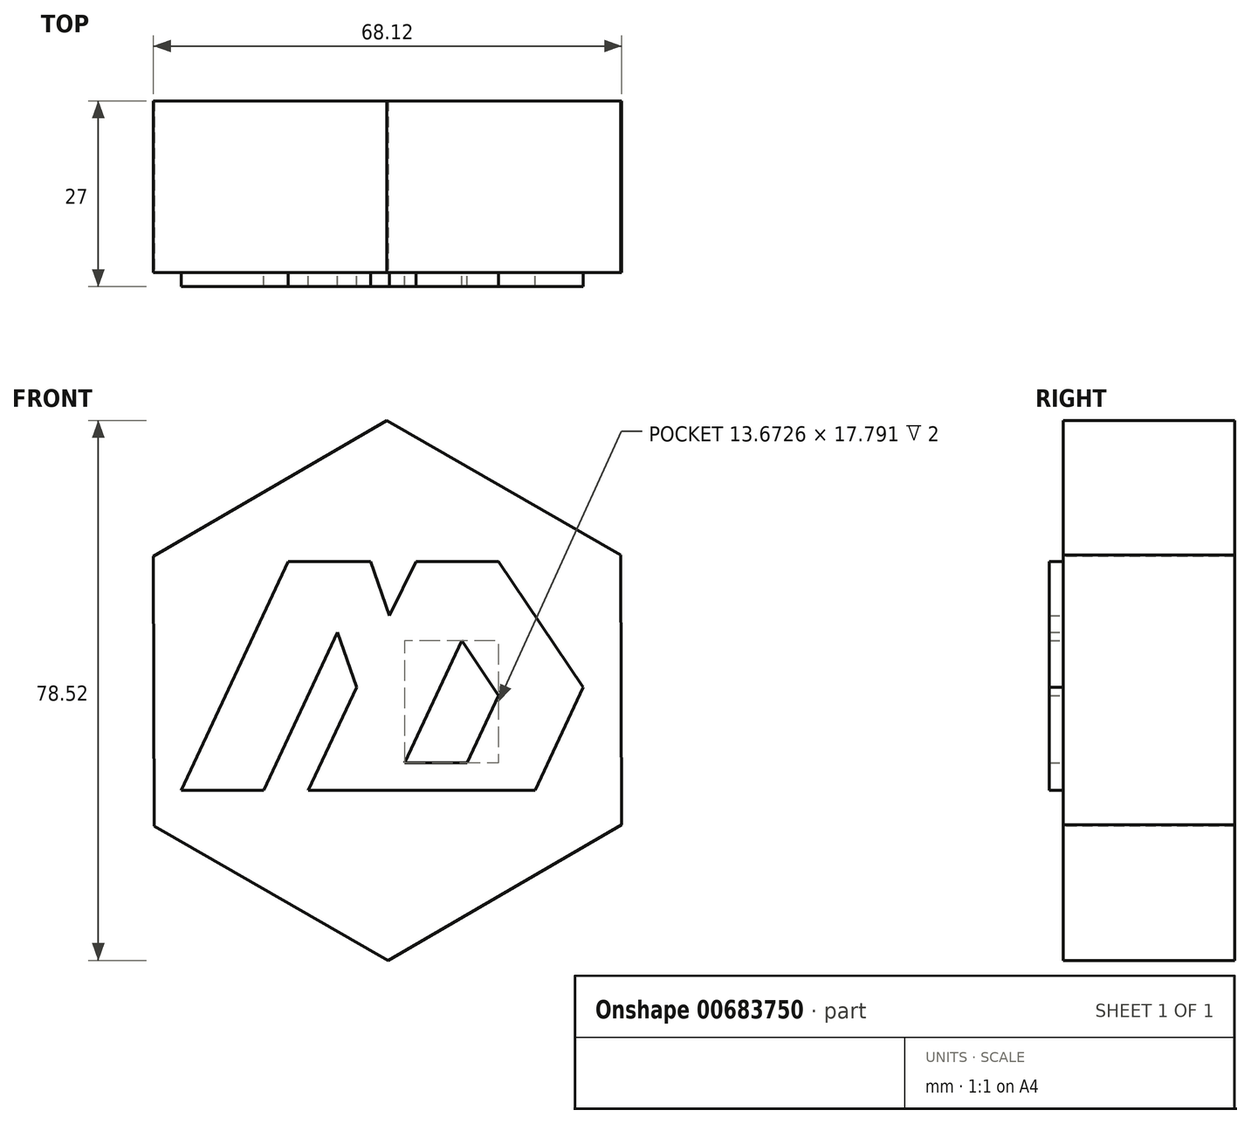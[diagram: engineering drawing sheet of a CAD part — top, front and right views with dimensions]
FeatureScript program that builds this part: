
annotation { "Feature Type Name" : "Feature", "Feature Type Description" : "" }
export const myFeature = defineFeature(function(context is Context, id is Id, definition is map)
    precondition{}
    {
        {
            var Q0;
            Q0=qCreatedBy(makeId("Front.planeOp"),FACE);
            var sketch = newSketch(context, id + "F0", { "sketchPlane" : qUnion([Q0])});
            skLineSegment(sketch, "E0", {"start": v(0, 0) * mm, "end": v(12, 0) * mm});
            skLineSegment(sketch, "E1", {"start": v(12, 0) * mm, "end": v(22.73, 23) * mm});
            skLineSegment(sketch, "E2", {"start": v(22.73, 23) * mm, "end": v(25.5, 15) * mm});
            skLineSegment(sketch, "E3", {"start": v(25.5, 15) * mm, "end": v(18.5, 0) * mm});
            skLineSegment(sketch, "E4", {"start": v(18.5, 0) * mm, "end": v(51.5, 0) * mm});
            skLineSegment(sketch, "E5", {"start": v(51.5, 0) * mm, "end": v(58.5, 15) * mm});
            skLineSegment(sketch, "E6", {"start": v(58.5, 15) * mm, "end": v(46.17, 33.3) * mm});
            skLineSegment(sketch, "E7", {"start": v(46.17, 33.3) * mm, "end": v(34.17, 33.3) * mm});
            skLineSegment(sketch, "E8", {"start": v(34.17, 33.3) * mm, "end": v(30.26, 25.4) * mm});
            skLineSegment(sketch, "E9", {"start": v(30.26, 25.4) * mm, "end": v(27.53, 33.3) * mm});
            skLineSegment(sketch, "E10", {"start": v(27.53, 33.3) * mm, "end": v(15.53, 33.3) * mm});
            skLineSegment(sketch, "E11", {"start": v(15.53, 33.3) * mm, "end": v(0, 0) * mm});
            skLineSegment(sketch, "E12", {"start": v(32.5, 4) * mm, "end": v(41.6, 4) * mm});
            skLineSegment(sketch, "E13", {"start": v(41.6, 4) * mm, "end": v(46.17, 13.8) * mm});
            skLineSegment(sketch, "E14", {"start": v(46.17, 13.8) * mm, "end": v(40.8, 21.8) * mm});
            skLineSegment(sketch, "E15", {"start": v(40.8, 21.8) * mm, "end": v(32.5, 4) * mm});
            skCircle(sketch, "E16.cCircle", {"center": v(30, 14.54) * mm, "radius": 34 * mm, "construction": true});
            skLineSegment(sketch, "E16.0", {"start": v(29.87, 53.8) * mm, "end": v(63.93, 34.28) * mm});
            skLineSegment(sketch, "E16.1", {"start": v(63.93, 34.28) * mm, "end": v(64.06, -4.98) * mm});
            skLineSegment(sketch, "E16.2", {"start": v(64.06, -4.98) * mm, "end": v(30.12, -24.72) * mm});
            skLineSegment(sketch, "E16.3", {"start": v(30.12, -24.72) * mm, "end": v(-3.94, -5.2) * mm});
            skLineSegment(sketch, "E16.4", {"start": v(-3.94, -5.2) * mm, "end": v(-4.06, 34.06) * mm});
            skLineSegment(sketch, "E16.5", {"start": v(-4.06, 34.06) * mm, "end": v(29.87, 53.8) * mm});
            skPoint(sketch, "E16.0.midPoint", {"position": v(46.9, 44.04) * mm});
            skSolve(sketch);
        }
        {
            var Q0;
            Q0=makeQuery(id+"F0.imprint","IMPRINT",FACE,{"disambiguationData":[TD([[makeQuery(id+"F0.imprint","IMPRINT",EDGE,{"derivedFrom":sQuery(id+"F0.wireOp",EDGE,"E0")}),1.0]])]});
            var Q1;
            Q1=makeQuery(id+"F0.imprint","IMPRINT",FACE,{"disambiguationData":[TD([[makeQuery(id+"F0.imprint","IMPRINT",EDGE,{"derivedFrom":sQuery(id+"F0.wireOp",EDGE,"E0")}),-1.0]])]});
            var Q2;
            Q2=makeQuery(id+"F0.imprint","IMPRINT",FACE,{"disambiguationData":[TD([[makeQuery(id+"F0.imprint","IMPRINT",EDGE,{"derivedFrom":sQuery(id+"F0.wireOp",EDGE,"E12")}),1.0]])]});
            extrude(context, id + "F1", {"entities" : qUnion([Q0, Q1, Q2]), "oppositeDirection" : true, "depth" : 25 * mm, "offsetDistance" : 25 * mm});
        }
        {
            var Q0;
            Q0=makeQuery(id+"F0.imprint","IMPRINT",FACE,{"disambiguationData":[TD([[makeQuery(id+"F0.imprint","IMPRINT",EDGE,{"derivedFrom":sQuery(id+"F0.wireOp",EDGE,"E0")}),1.0]])]});
            extrude(context, id + "F2", {"entities" : qUnion([Q0]), "operationType" : NewBodyOperationType.ADD, "depth" : 2 * mm, "offsetDistance" : 25 * mm});
        }
    });
